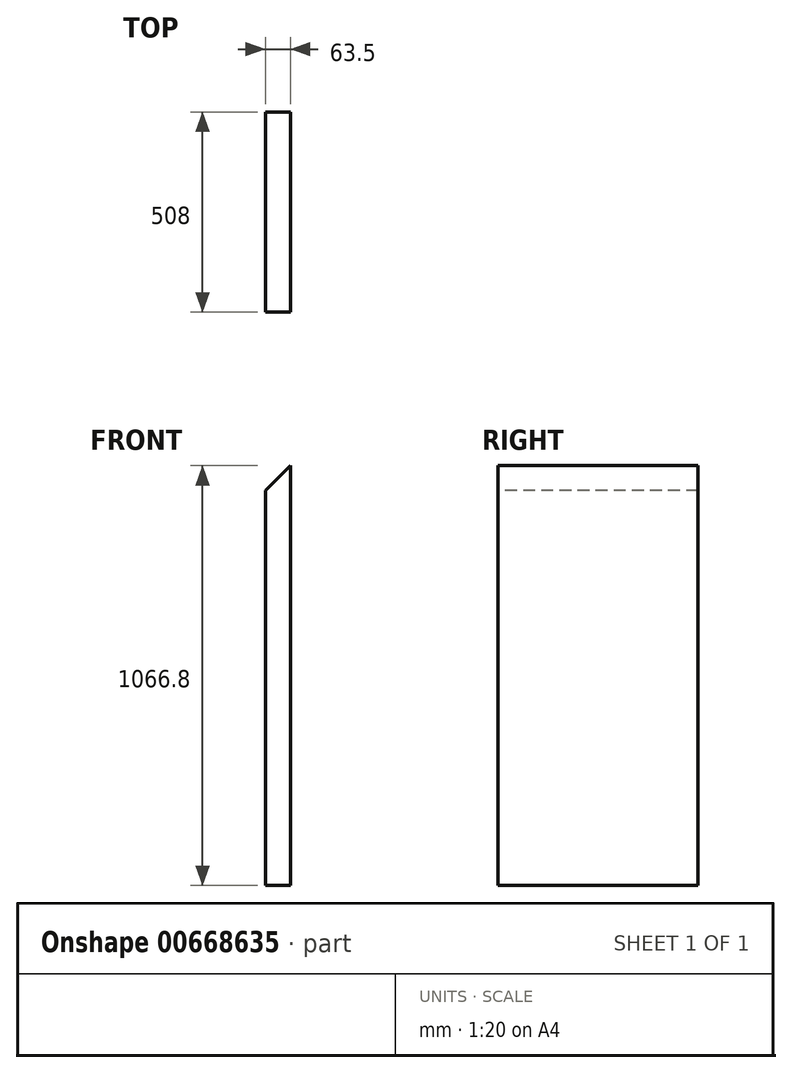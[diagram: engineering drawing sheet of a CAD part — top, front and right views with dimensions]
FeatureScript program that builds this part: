
annotation { "Feature Type Name" : "Feature", "Feature Type Description" : "" }
export const myFeature = defineFeature(function(context is Context, id is Id, definition is map)
    precondition{}
    {
        {
            var Q0;
            Q0=qCreatedBy(makeId("Right.planeOp"),FACE);
            var sketch = newSketch(context, id + "F0", { "sketchPlane" : qUnion([Q0])});
            skLineSegment(sketch, "E0.bottom", {"start": v(-254, 533.4) * mm, "end": v(254, 533.4) * mm});
            skLineSegment(sketch, "E0.top", {"start": v(-254, -533.4) * mm, "end": v(254, -533.4) * mm});
            skLineSegment(sketch, "E0.left", {"start": v(-254, 533.4) * mm, "end": v(-254, -533.4) * mm});
            skLineSegment(sketch, "E0.right", {"start": v(254, 533.4) * mm, "end": v(254, -533.4) * mm});
            skSolve(sketch);
        }
        {
            var Q0;
            Q0 = qSketchRegion(id + "F0", true);
            extrude(context, id + "F1", {"entities" : qUnion([Q0]), "depth" : 63.5 * mm, "offsetDistance" : 25.4 * mm, "symmetric" : true});
        }
        {
            var Q0;
            Q0=makeQuery(id+"F1.opExtrude","SWEPT_FACE",FACE,{"disambiguationData":[OSD([sQuery(id+"F0.wireOp",EDGE,"E0.left")])]});
            var sketch = newSketch(context, id + "F2", { "sketchPlane" : qUnion([Q0])});
            skLineSegment(sketch, "E1", {"start": v(31.75, 533.4) * mm, "end": v(-31.75, 533.4) * mm});
            skLineSegment(sketch, "E2", {"start": v(-31.75, 533.4) * mm, "end": v(-31.75, 469.9) * mm});
            skLineSegment(sketch, "E3", {"start": v(-31.75, 469.9) * mm, "end": v(31.75, 533.4) * mm});
            skSolve(sketch);
        }
        {
            var Q0;
            Q0 = qSketchRegion(id + "F2", true);
            extrude(context, id + "F3", {"entities" : qUnion([Q0]), "operationType" : NewBodyOperationType.REMOVE, "endBound" : BoundingType.THROUGH_ALL, "oppositeDirection" : true, "depth" : 25.4 * mm, "offsetDistance" : 25.4 * mm});
        }
    });
